# Revit family: Секция водяного нагрева вместе с водяным охлаждением AIRNED-M Т1
name_source: partatom
category: Оборудование
revit_build: Autodesk Revit 2017 (Build: 20160225_1515(x64)
units: mm (PartAtom-declared; Revit-internal decimal feet)

## family parameters
Всегда вертикально = Да
На основе рабочей плоскости = Нет
Общий = Нет
При загрузке вырезать с полостями = Нет
Размер круглого соединителя = Использовать диаметр
Тип детали = Нормальный
Точка расчета площади = Нет

## types (20) — shared parameters
h = 130 мм
Д = 1100 мм
Д1 = 1080 мм
Единица измерения = шт.
Завод изготовитель = NED
Ключевая пометка = Вентиляция
Материал = Сталь серая
Наименование и тех.хар-ка = Секция водяного нагрева вместе с водяным охлаждением
Раздел = ОВ
высота ножек = 120 мм

## per-type parameters (varying)
| type | d | А | А1 | Б | Б1 | Вн | Во | Высота | Гн | И | Середина | Ширина |
| AIRNED-M 6 T1.3 | 32 мм | 1100 мм | 1080 мм | 1100 мм | 1080 мм | 735 мм | 728 мм | 1025 мм | 85 мм | 135 мм | 670 мм | 1025 мм |
| AIRNED-M 7 T1.3 | 38 мм | 1100 мм | 1080 мм | 1320 мм | 1300 мм | 985 мм | 985 мм | 1245 мм | 85 мм | 115 мм | 780 мм | 1025 мм |
| AIRNED-M 8 T1.3 | 38 мм | 1320 мм | 1300 мм | 1320 мм | 1300 мм | 985 мм | 985 мм | 1245 мм | 85 мм | 115 мм | 780 мм | 1245 мм |
| AIRNED-M 12 T1.3 | 51 мм | 1435 мм | 1415 мм | 1435 мм | 1415 мм | 1060 мм | 1060 мм | 1360 мм | 85 мм | 115 мм | 838 мм | 1360 мм |
| AIRNED-M 20 T1.3 | 51 мм | 1660 мм | 1640 мм | 1660 мм | 1640 мм | 1355 мм | 1305 мм | 1585 мм | 85 мм | 115 мм | 950 мм | 1585 мм |
| AIRNED-M 25 T1.3 | 64 мм | 2045 мм | 2025 мм | 2045 мм | 2025 мм | 1740 мм | 1690 мм | 1970 мм | 85 мм | 115 мм | 1143 мм | 1970 мм |
| AIRNED-M 30 T1.3 | 64 мм | 2485 мм | 2465 мм | 2045 мм | 2025 мм | 1685 мм | 1685 мм | 1970 мм | 100 мм | 115 мм | 1143 мм | 2410 мм |
| AIRNED-M 35 T1.3 | 76 мм | 2485 мм | 2465 мм | 2485 мм | 2465 мм | 2125 мм | 2125 мм | 2410 мм | 125 мм | 115 мм | 1363 мм | 2410 мм |
| AIRNED-M 40 T1.3 | 102 мм | 3320 мм | 3300 мм | 3320 мм | 3300 мм | 1355 мм | 1305 мм | 3245 мм | 100 мм | 115 мм | 1780 мм | 3245 мм |
| AIRNED-M 45 T1.3 | 102 мм | 3320 мм | 3300 мм | 4090 мм | 4070 мм | 1740 мм | 1690 мм | 4015 мм | 125 мм | 115 мм | 2165 мм | 3245 мм |
| AIRNED-M 6 T1.4 | 38 мм | 1100 мм | 1080 мм | 1100 мм | 1080 мм | 722 мм | 735 мм | 1025 мм | 85 мм | 115 мм | 670 мм | 1025 мм |
| AIRNED-M 7 T1.4 | 38 мм | 1100 мм | 1080 мм | 1320 мм | 1300 мм | 972 мм | 985 мм | 1245 мм | 85 мм | 115 мм | 780 мм | 1025 мм |
| AIRNED-M 8 T1.4 | 51 мм | 1320 мм | 1300 мм | 1320 мм | 1300 мм | 985 мм | 985 мм | 1245 мм | 85 мм | 115 мм | 780 мм | 1245 мм |
| AIRNED-M 12 T1.4 | 51 мм | 1435 мм | 1415 мм | 1435 мм | 1415 мм | 1152 мм | 1083 мм | 1360 мм | 85 мм | 115 мм | 838 мм | 1360 мм |
| AIRNED-M 20 T1.4 | 64 мм | 1660 мм | 1640 мм | 1660 мм | 1640 мм | 1355 мм | 1290 мм | 1585 мм | 85 мм | 115 мм | 950 мм | 1585 мм |
| AIRNED-M 25 T1.4 | 76 мм | 2045 мм | 2025 мм | 2045 мм | 2025 мм | 1740 мм | 1690 мм | 1970 мм | 85 мм | 115 мм | 1143 мм | 1970 мм |
| AIRNED-M 30 T1.4 | 76 мм | 2485 мм | 2465 мм | 2045 мм | 2025 мм | 1685 мм | 1685 мм | 1970 мм | 100 мм | 115 мм | 1143 мм | 2410 мм |
| AIRNED-M 35 T1.4 | 102 мм | 2485 мм | 2465 мм | 2485 мм | 2465 мм | 2100 мм | 2100 мм | 2410 мм | 125 мм | 115 мм | 1363 мм | 2410 мм |
| AIRNED-M 40 T1.4 | 102 мм | 3320 мм | 3300 мм | 3320 мм | 3300 мм | 1355 мм | 1290 мм | 3245 мм | 100 мм | 115 мм | 1780 мм | 3245 мм |
| AIRNED-M 45 T1.4 | 102 мм | 3320 мм | 3300 мм | 4090 мм | 4070 мм | 1740 мм | 1690 мм | 4015 мм | 125 мм | 115 мм | 2165 мм | 3245 мм |

note: column(s) folded — value = type name in every type: Тип, марка, обозначение
